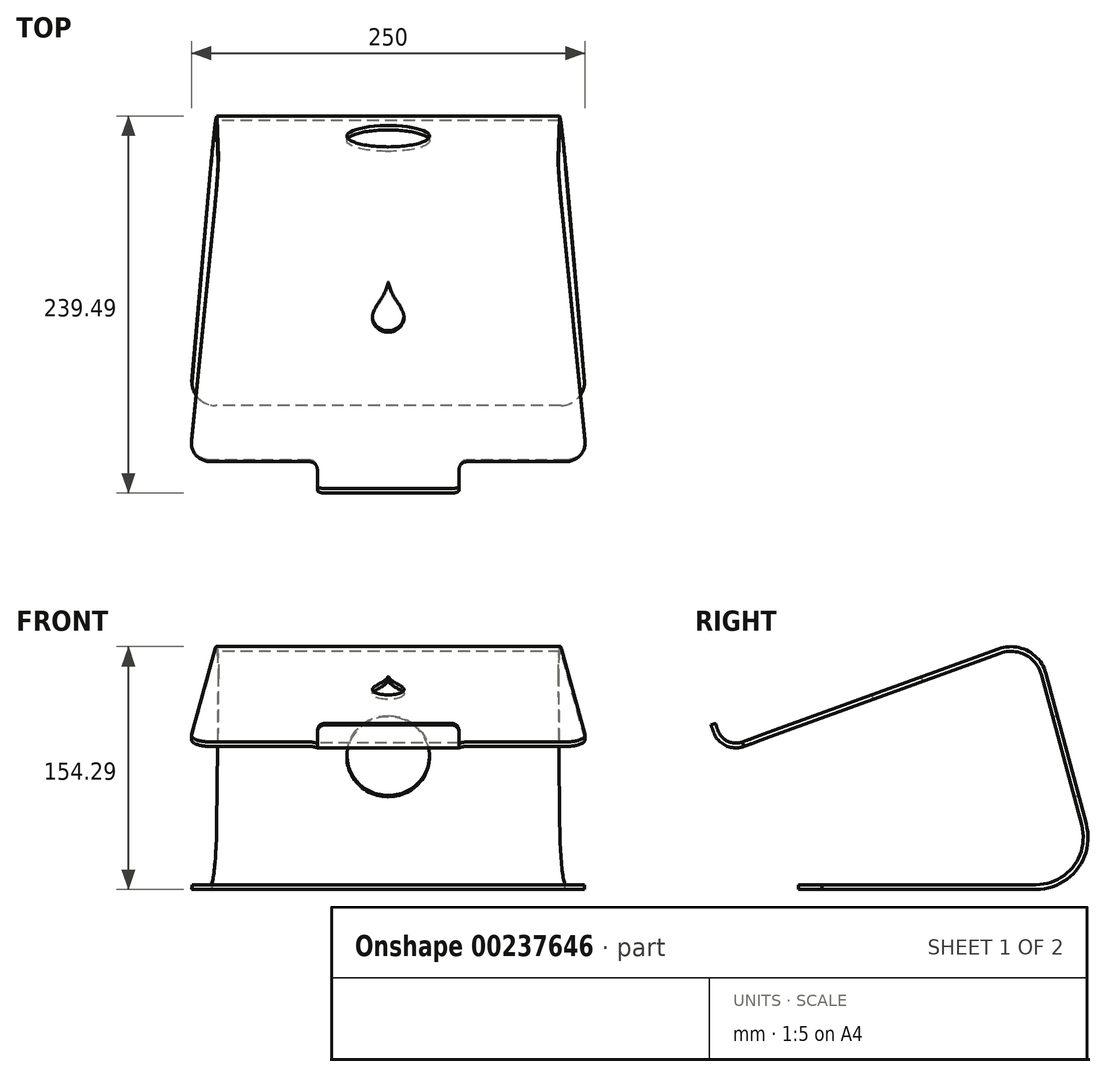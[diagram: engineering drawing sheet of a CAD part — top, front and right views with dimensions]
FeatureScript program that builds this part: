
annotation { "Feature Type Name" : "Feature", "Feature Type Description" : "" }
export const myFeature = defineFeature(function(context is Context, id is Id, definition is map)
    precondition{}
    {
        {
            var Q0;
            Q0=qCreatedBy(makeId("Right.planeOp"),FACE);
            var sketch = newSketch(context, id + "F0", { "sketchPlane" : qUnion([Q0])});
            skLineSegment(sketch, "E0", {"start": v(0, 0) * mm, "end": v(150.9, 0) * mm});
            skLineSegment(sketch, "E1", {"start": v(179.88, 37.76) * mm, "end": v(154.24, 133.47) * mm});
            skLineSegment(sketch, "E2", {"start": v(128.08, 147.08) * mm, "end": v(-34.65, 87.85) * mm});
            skLineSegment(sketch, "E3", {"start": v(-53.88, 96.82) * mm, "end": v(-55.59, 101.52) * mm});
            skPoint(sketch, "E4.visualSharp", {"position": v(190, 0) * mm});
            skArc(sketch, "E4.filletArc", {"start": v(150.9, 0) * mm, "mid": v(174.7, 11.74) * mm, "end": v(179.88, 37.76) * mm});
            skPoint(sketch, "E5.visualSharp", {"position": v(148.59, 154.55) * mm});
            skArc(sketch, "E5.filletArc", {"start": v(154.24, 133.47) * mm, "mid": v(144.15, 146.03) * mm, "end": v(128.08, 147.08) * mm});
            skPoint(sketch, "E6.visualSharp", {"position": v(-48.75, 82.72) * mm});
            skArc(sketch, "E6.filletArc", {"start": v(-53.88, 96.82) * mm, "mid": v(-46.12, 88.35) * mm, "end": v(-34.65, 87.85) * mm});
            skLineSegment(sketch, "E7.0", {"start": v(-51.06, 97.85) * mm, "end": v(-52.77, 102.54) * mm});
            skArc(sketch, "E7.1", {"start": v(-51.06, 97.85) * mm, "mid": v(-44.85, 91.07) * mm, "end": v(-35.68, 90.67) * mm});
            skLineSegment(sketch, "E7.2", {"start": v(127.05, 149.9) * mm, "end": v(-35.68, 90.67) * mm});
            skLineSegment(sketch, "E7.3", {"start": v(0, -3) * mm, "end": v(150.9, -3) * mm});
            skArc(sketch, "E7.4", {"start": v(150.9, -3) * mm, "mid": v(177.08, 9.91) * mm, "end": v(182.78, 38.54) * mm});
            skLineSegment(sketch, "E7.5", {"start": v(182.78, 38.54) * mm, "end": v(157.14, 134.24) * mm});
            skArc(sketch, "E7.6", {"start": v(157.14, 134.24) * mm, "mid": v(145.54, 148.7) * mm, "end": v(127.05, 149.9) * mm});
            skLineSegment(sketch, "E8", {"start": v(0, 0) * mm, "end": v(0, -3) * mm});
            skLineSegment(sketch, "E9", {"start": v(-52.77, 102.54) * mm, "end": v(-55.59, 101.52) * mm});
            skSolve(sketch);
        }
        {
            var Q0;
            Q0 = qSketchRegion(id + "F0", true);
            extrude(context, id + "F1", {"entities" : qUnion([Q0]), "depth" : (125 * 2) * mm, "symmetric" : true});
        }
        {
            var Q0;
            Q0=makeQuery(id+"F1.opExtrude","SWEPT_FACE",FACE,{"disambiguationData":[OSD([sQuery(id+"F0.wireOp",EDGE,"E7.5")])]});
            var sketch = newSketch(context, id + "F2", { "sketchPlane" : qUnion([Q0])});
            skCircle(sketch, "E10", {"center": v(0, 35) * mm, "radius": 26.25 * mm});
            skSolve(sketch);
        }
        {
            var Q0;
            Q0 = qSketchRegion(id + "F2", true);
            extrude(context, id + "F3", {"entities" : qUnion([Q0]), "operationType" : NewBodyOperationType.REMOVE, "oppositeDirection" : true, "depth" : 25 * mm});
        }
        {
            var Q0;
            Q0=makeQuery(id+"F1.opExtrude","SWEPT_FACE",FACE,{"disambiguationData":[OSD([sQuery(id+"F0.wireOp",EDGE,"E7.2")])]});
            var sketch = newSketch(context, id + "F4", { "sketchPlane" : qUnion([Q0])});
            skLineSegment(sketch, "E11", {"start": v(0, 104.76) * mm, "end": v(0, -25.38) * mm, "construction": true});
            skPoint(sketch, "E11.endSnap0", {"position": v(0, -2.51) * mm});
            skLineSegment(sketch, "E12", {"start": v(0, -25.38) * mm, "end": v(131.7, -25.38) * mm, "construction": true});
            skLineSegment(sketch, "E13.bottom", {"start": v(45, -2.51) * mm, "end": v(142.61, -2.51) * mm});
            skLineSegment(sketch, "E13.top", {"start": v(45, -19.61) * mm, "end": v(142.61, -19.61) * mm});
            skLineSegment(sketch, "E13.left", {"start": v(45, -2.51) * mm, "end": v(45, -19.61) * mm});
            skLineSegment(sketch, "E13.right", {"start": v(142.61, -2.51) * mm, "end": v(142.61, -19.61) * mm});
            skLineSegment(sketch, "E14.MirrorCS", {"start": v(-45, -2.51) * mm, "end": v(-45, -19.61) * mm});
            skLineSegment(sketch, "E15.MirrorCS", {"start": v(-45, -2.51) * mm, "end": v(-142.61, -2.51) * mm});
            skLineSegment(sketch, "E16.MirrorCS", {"start": v(-45, -19.61) * mm, "end": v(-142.61, -19.61) * mm});
            skLineSegment(sketch, "E17.MirrorCS", {"start": v(-142.61, -2.51) * mm, "end": v(-142.61, -19.61) * mm});
            skSolve(sketch);
        }
        {
            var Q0;
            Q0 = qSketchRegion(id + "F4", true);
            extrude(context, id + "F5", {"entities" : qUnion([Q0]), "operationType" : NewBodyOperationType.REMOVE, "depth" : 45 * mm, "symmetric" : true});
        }
        {
            var Q0;
            Q0=makeQuery(id+"F1.opExtrude","SWEPT_FACE",FACE,{"disambiguationData":[OSD([sQuery(id+"F0.wireOp",EDGE,"E7.2")])]});
            var sketch = newSketch(context, id + "F6", { "sketchPlane" : qUnion([Q0])});
            skLineSegment(sketch, "E18", {"start": v(0, 0) * mm, "end": v(0, 170.66) * mm, "construction": true});
            skLineSegment(sketch, "E19", {"start": v(-110, 170.66) * mm, "end": v(-124.95, 11.15) * mm});
            skLineSegment(sketch, "E20", {"start": v(-110, 170.66) * mm, "end": v(-110, 62.24) * mm, "construction": true});
            skArc(sketch, "E21", {"start": v(-124.95, 11.15) * mm, "mid": v(-121.74, 1.57) * mm, "end": v(-112.5, -2.51) * mm});
            skLineSegment(sketch, "E22", {"start": v(-110, 170.66) * mm, "end": v(-107.16, 200.95) * mm});
            skLineSegment(sketch, "E23", {"start": v(-107.16, 200.95) * mm, "end": v(-152.58, 200.95) * mm});
            skLineSegment(sketch, "E24", {"start": v(-152.58, 200.95) * mm, "end": v(-152.58, -22.45) * mm});
            skLineSegment(sketch, "E25", {"start": v(-152.58, -22.45) * mm, "end": v(-112.5, -22.45) * mm});
            skLineSegment(sketch, "E26", {"start": v(-112.5, -22.45) * mm, "end": v(-112.5, -2.51) * mm});
            skLineSegment(sketch, "E27.MirrorCS", {"start": v(112.5, -22.45) * mm, "end": v(112.5, -2.51) * mm});
            skArc(sketch, "E28.MirrorCS", {"start": v(124.95, 11.15) * mm, "mid": v(121.74, 1.57) * mm, "end": v(112.5, -2.51) * mm});
            skLineSegment(sketch, "E29.MirrorCS", {"start": v(110, 170.66) * mm, "end": v(124.95, 11.15) * mm});
            skLineSegment(sketch, "E30.MirrorCS", {"start": v(110, 170.66) * mm, "end": v(107.16, 200.95) * mm});
            skLineSegment(sketch, "E31.MirrorCS", {"start": v(107.16, 200.95) * mm, "end": v(152.58, 200.95) * mm});
            skLineSegment(sketch, "E32.MirrorCS", {"start": v(152.58, 200.95) * mm, "end": v(152.58, -22.45) * mm});
            skLineSegment(sketch, "E33.MirrorCS", {"start": v(152.58, -22.45) * mm, "end": v(112.5, -22.45) * mm});
            skSolve(sketch);
        }
        {
            var Q0;
            Q0 = qSketchRegion(id + "F6", true);
            extrude(context, id + "F7", {"entities" : qUnion([Q0]), "operationType" : NewBodyOperationType.REMOVE, "oppositeDirection" : true, "depth" : 223 * mm});
        }
        {
            var Q0;
            Q0=makeQuery(id+"F1.opExtrude","SWEPT_FACE",FACE,{"disambiguationData":[OSD([sQuery(id+"F0.wireOp",EDGE,"E7.3")])]});
            var sketch = newSketch(context, id + "F8", { "sketchPlane" : qUnion([Q0])});
            skArc(sketch, "E34", {"start": v(-109.7, 0) * mm, "mid": v(-120.31, -4.4) * mm, "end": v(-124.7, -15) * mm});
            skLineSegment(sketch, "E35", {"start": v(-109.7, 1.84) * mm, "end": v(-109.7, 0) * mm});
            skPoint(sketch, "E35.endSnap0", {"position": v(-109.7, 1.84) * mm});
            skLineSegment(sketch, "E36", {"start": v(-124.7, -15) * mm, "end": v(-139.14, -15) * mm});
            skLineSegment(sketch, "E37", {"start": v(-139.14, -15) * mm, "end": v(-139.14, 2.55) * mm});
            skLineSegment(sketch, "E38", {"start": v(-139.14, 2.55) * mm, "end": v(-109.7, 1.84) * mm});
            skPoint(sketch, "E39.end.orphan", {"position": v(-109.7, 36.52) * mm});
            skLineSegment(sketch, "E40", {"start": v(0, 0) * mm, "end": v(0, -75.44) * mm, "construction": true});
            skPoint(sketch, "E40.endSnap0", {"position": v(0, 0) * mm});
            skArc(sketch, "E41.MirrorCS", {"start": v(109.7, 0) * mm, "mid": v(120.31, -4.4) * mm, "end": v(124.7, -15) * mm});
            skLineSegment(sketch, "E42.MirrorCS", {"start": v(124.7, -15) * mm, "end": v(139.14, -15) * mm});
            skLineSegment(sketch, "E43.MirrorCS", {"start": v(139.14, -15) * mm, "end": v(139.14, 2.55) * mm});
            skLineSegment(sketch, "E44.MirrorCS", {"start": v(139.14, 2.55) * mm, "end": v(109.7, 1.84) * mm});
            skLineSegment(sketch, "E45.MirrorCS", {"start": v(109.7, 1.84) * mm, "end": v(109.7, 0) * mm});
            skSolve(sketch);
        }
        {
            var Q0;
            Q0 = qSketchRegion(id + "F8", true);
            extrude(context, id + "F9", {"entities" : qUnion([Q0]), "operationType" : NewBodyOperationType.REMOVE, "oppositeDirection" : true, "depth" : 25 * mm});
        }
        {
            var Q0;
            Q0=makeQuery(id+"F5.boolean.opBoolean","COPY",EDGE,{"derivedFrom":makeQuery(id+"F5.opExtrude","SWEPT_EDGE",EDGE,{"disambiguationData":[OSD([sQuery(id+"F0.wireOp",EDGE,"E7.1"),sQuery(id+"F0.wireOp",EDGE,"E7.2"),sQuery(id+"F4.wireOp",EDGE,"E14.MirrorCS"),sQuery(id+"F4.wireOp",EDGE,"E15.MirrorCS")])]})});
            var Q1;
            Q1=makeQuery(id+"F5.boolean.opBoolean","COPY",EDGE,{"derivedFrom":makeQuery(id+"F5.opExtrude","SWEPT_EDGE",EDGE,{"disambiguationData":[OSD([sQuery(id+"F0.wireOp",EDGE,"E7.1"),sQuery(id+"F0.wireOp",EDGE,"E7.2"),sQuery(id+"F4.wireOp",EDGE,"E13.bottom"),sQuery(id+"F4.wireOp",EDGE,"E13.left")])]})});
            var Q2;
            Q2=makeQuery(id+"F5.boolean.opBoolean","INTERSECT",EDGE,{"derivedFrom":[makeQuery(id+"F1.opExtrude","SWEPT_FACE",FACE,{"disambiguationData":[OSD([sQuery(id+"F0.wireOp",EDGE,"E9")])]}),makeQuery(id+"F5.opExtrude","SWEPT_FACE",FACE,{"disambiguationData":[OSD([sQuery(id+"F4.wireOp",EDGE,"E13.left")])]})]});
            var Q3;
            Q3=makeQuery(id+"F5.boolean.opBoolean","INTERSECT",EDGE,{"derivedFrom":[makeQuery(id+"F1.opExtrude","SWEPT_FACE",FACE,{"disambiguationData":[OSD([sQuery(id+"F0.wireOp",EDGE,"E9")])]}),makeQuery(id+"F5.opExtrude","SWEPT_FACE",FACE,{"disambiguationData":[OSD([sQuery(id+"F4.wireOp",EDGE,"E14.MirrorCS")])]})]});
            fillet(context, id + "F10", {"entities" : qUnion([Q0, Q1, Q2, Q3]), "radius" : 5 * mm, "tangentPropagation" : true, "allowEdgeOverflow" : false});
        }
        {
            var Q0;
            Q0=makeQuery(id+"F1.opExtrude","SWEPT_FACE",FACE,{"disambiguationData":[OSD([sQuery(id+"F0.wireOp",EDGE,"E7.2")])]});
            var sketch = newSketch(context, id + "F11", { "sketchPlane" : qUnion([Q0])});
            skLineSegment(sketch, "E46", {"start": v(0, 145) * mm, "end": v(0, 95) * mm, "construction": true});
            skLineSegment(sketch, "E47", {"start": v(0, 95) * mm, "end": v(44.17, 95) * mm, "construction": true});
            skArc(sketch, "E48", {"start": v(0, 85) * mm, "mid": v(8.04, 89.06) * mm, "end": v(9.56, 97.94) * mm});
            skFitSpline(sketch, "E49", {"points": [v(0, 120) * mm, v(9.56, 97.94) * mm], "startDerivative": vector(3.28, -31.5) * mm, "endDerivative": vector(6.7, -21.79) * mm});
            skLineSegment(sketch, "E50", {"start": v(0, 95) * mm, "end": v(0, 81.22) * mm, "construction": true});
            skFitSpline(sketch, "E51.MirrorCS", {"points": [v(0, 120) * mm, v(-9.56, 97.94) * mm], "startDerivative": vector(-3.28, -31.5) * mm, "endDerivative": vector(-6.7, -21.79) * mm});
            skArc(sketch, "E52.MirrorCS", {"start": v(0, 85) * mm, "mid": v(-8.04, 89.06) * mm, "end": v(-9.56, 97.94) * mm});
            skArc(sketch, "E53.filletArc", {"start": v(0.25, 118.2) * mm, "mid": v(0, 118.4) * mm, "end": v(-0.25, 118.2) * mm});
            skSolve(sketch);
        }
        {
            var Q0;
            Q0=makeQuery(id+"F11.imprint","IMPRINT",FACE,{"disambiguationData":[TD([[makeQuery(id+"F11.imprint","IMPRINT",EDGE,{"derivedFrom":sQuery(id+"F11.wireOp",EDGE,"E48")}),1.0]])]});
            extrude(context, id + "F12", {"entities" : qUnion([Q0]), "operationType" : NewBodyOperationType.REMOVE, "oppositeDirection" : true, "depth" : 25 * mm});
        }
    });
